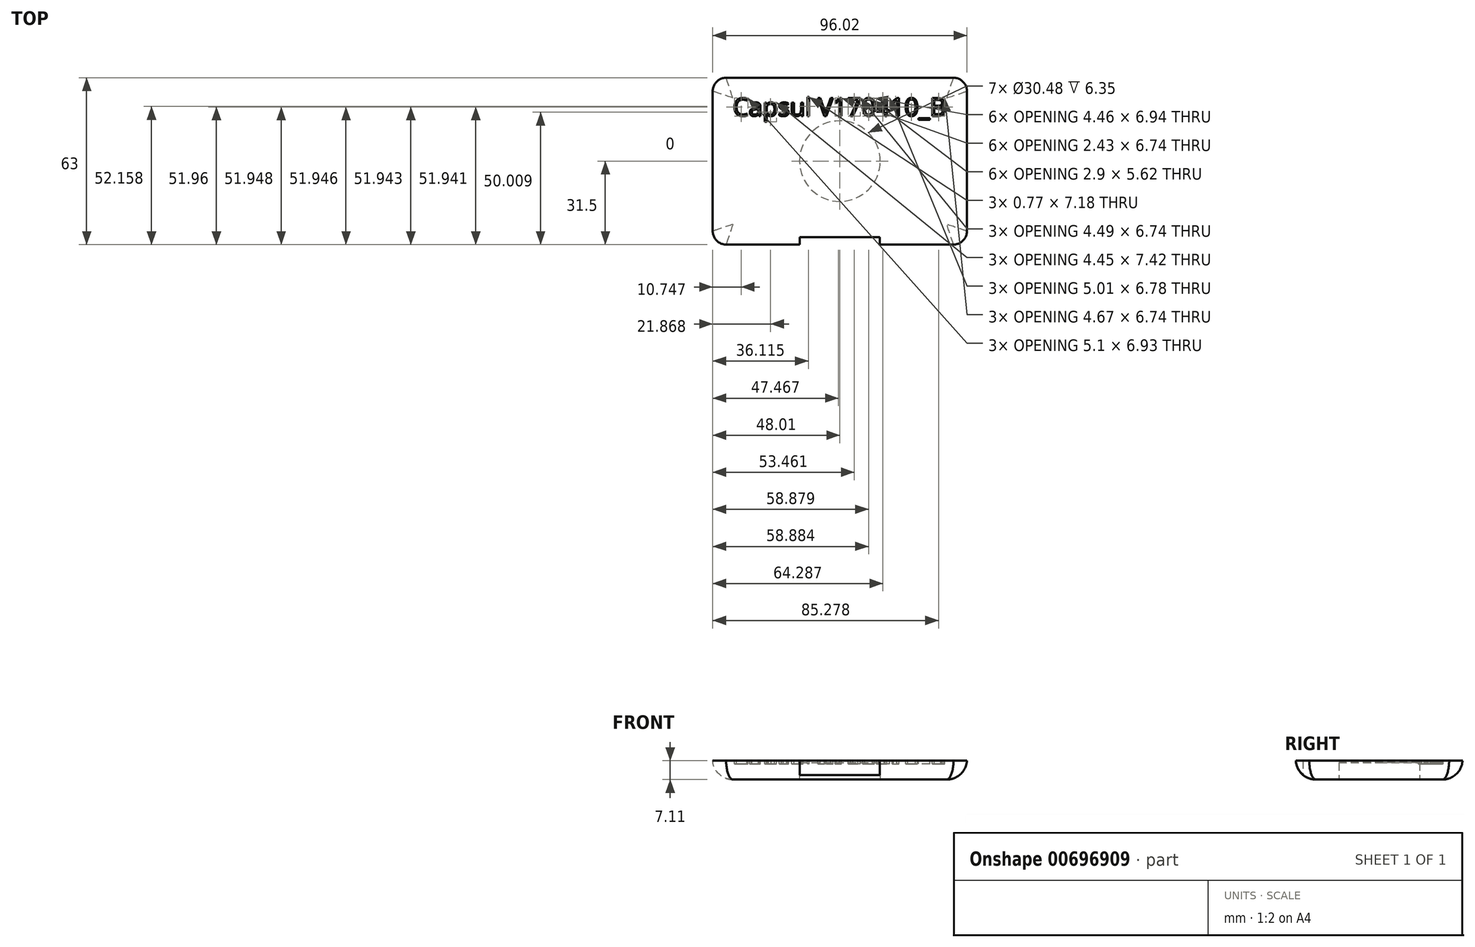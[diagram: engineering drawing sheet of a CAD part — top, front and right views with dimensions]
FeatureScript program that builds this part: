
annotation { "Feature Type Name" : "Feature", "Feature Type Description" : "" }
export const myFeature = defineFeature(function(context is Context, id is Id, definition is map)
    precondition{}
    {
        {
            var Q0;
            Q0=qCreatedBy(makeId("Top.planeOp"),FACE);
            var sketch = newSketch(context, id + "F0", { "sketchPlane" : qUnion([Q0])});
            skLineSegment(sketch, "E0.bottom", {"start": v(48, 31.5) * mm, "end": v(-48, 31.5) * mm});
            skLineSegment(sketch, "E0.top", {"start": v(48, -31.5) * mm, "end": v(-48, -31.5) * mm});
            skLineSegment(sketch, "E0.left", {"start": v(48, 31.5) * mm, "end": v(48, -31.5) * mm});
            skLineSegment(sketch, "E0.right", {"start": v(-48, 31.5) * mm, "end": v(-48, -31.5) * mm});
            skPoint(sketch, "E0.middle", {"position": v(0, 0) * mm});
            skSolve(sketch);
        }
        {
            var Q0;
            Q0=makeQuery(id+"F0.imprint","IMPRINT",FACE,{"disambiguationData":[TD([[makeQuery(id+"F0.imprint","IMPRINT",EDGE,{"derivedFrom":sQuery(id+"F0.wireOp",EDGE,"E0.bottom")}),1.0]])]});
            extrude(context, id + "F1", {"entities" : qUnion([Q0]), "depth" : 7.11 * mm, "offsetDistance" : 25.4 * mm});
        }
        {
            var Q0;
            Q0=makeQuery(id+"F1.opExtrude","CAP_FACE",FACE,{"disambiguationData":[OSD([sQuery(id+"F0.wireOp",EDGE,"E0.bottom"),sQuery(id+"F0.wireOp",EDGE,"E0.top"),sQuery(id+"F0.wireOp",EDGE,"E0.left"),sQuery(id+"F0.wireOp",EDGE,"E0.right")])],"isStart":true});
            fillet(context, id + "F2", {"entities" : qUnion([Q0]), "radius" : 7.62 * mm, "tangentPropagation" : true, "allowEdgeOverflow" : false});
        }
        {
            var Q0;
            Q0=makeQuery(id+"F2.opFillet","BLEND_EDGE",EDGE,{"blendedFrom":[makeQuery(id+"F1.opExtrude","CAP_EDGE",EDGE,{"disambiguationData":[OSD([sQuery(id+"F0.wireOp",EDGE,"E0.bottom")])],"isStart":true}),makeQuery(id+"F1.opExtrude","CAP_EDGE",EDGE,{"disambiguationData":[OSD([sQuery(id+"F0.wireOp",EDGE,"E0.right")])],"isStart":true})],"blendedInto":[]});
            var Q1;
            Q1=makeQuery(id+"F2.opFillet","BLEND_EDGE",EDGE,{"blendedFrom":[makeQuery(id+"F1.opExtrude","CAP_EDGE",EDGE,{"disambiguationData":[OSD([sQuery(id+"F0.wireOp",EDGE,"E0.top")])],"isStart":true}),makeQuery(id+"F1.opExtrude","CAP_EDGE",EDGE,{"disambiguationData":[OSD([sQuery(id+"F0.wireOp",EDGE,"E0.right")])],"isStart":true})],"blendedInto":[]});
            var Q2;
            Q2=makeQuery(id+"F2.opFillet","BLEND_EDGE",EDGE,{"blendedFrom":[makeQuery(id+"F1.opExtrude","CAP_EDGE",EDGE,{"disambiguationData":[OSD([sQuery(id+"F0.wireOp",EDGE,"E0.bottom")])],"isStart":true}),makeQuery(id+"F1.opExtrude","CAP_EDGE",EDGE,{"disambiguationData":[OSD([sQuery(id+"F0.wireOp",EDGE,"E0.left")])],"isStart":true})],"blendedInto":[]});
            var Q3;
            Q3=makeQuery(id+"F2.opFillet","BLEND_EDGE",EDGE,{"blendedFrom":[makeQuery(id+"F1.opExtrude","CAP_EDGE",EDGE,{"disambiguationData":[OSD([sQuery(id+"F0.wireOp",EDGE,"E0.top")])],"isStart":true}),makeQuery(id+"F1.opExtrude","CAP_EDGE",EDGE,{"disambiguationData":[OSD([sQuery(id+"F0.wireOp",EDGE,"E0.left")])],"isStart":true})],"blendedInto":[]});
            fillet(context, id + "F3", {"entities" : qUnion([Q0, Q1, Q2, Q3]), "radius" : 5.08 * mm, "tangentPropagation" : true, "allowEdgeOverflow" : false});
        }
        {
            var Q0;
            Q0=makeQuery(id+"F1.opExtrude","CAP_FACE",FACE,{"disambiguationData":[OSD([sQuery(id+"F0.wireOp",EDGE,"E0.bottom"),sQuery(id+"F0.wireOp",EDGE,"E0.top"),sQuery(id+"F0.wireOp",EDGE,"E0.left"),sQuery(id+"F0.wireOp",EDGE,"E0.right")])],"isStart":true});
            var sketch = newSketch(context, id + "F4", { "sketchPlane" : qUnion([Q0])});
            skCircle(sketch, "E1", {"center": v(0, 0) * mm, "radius": 15.24 * mm});
            skSolve(sketch);
        }
        {
            var Q0;
            Q0=qSketchRegion(id+"F4",true);
            extrude(context, id + "F5", {"entities" : qUnion([Q0]), "operationType" : NewBodyOperationType.REMOVE, "oppositeDirection" : true, "depth" : 6.35 * mm, "offsetDistance" : 25.4 * mm});
        }
        {
            var Q0;
            Q0=qCreatedBy(makeId("Top.planeOp"),FACE);
            var sketch = newSketch(context, id + "F6", { "sketchPlane" : qUnion([Q0])});
            skLineSegment(sketch, "E2.bottom", {"start": v(15.15, -28.75) * mm, "end": v(-15.15, -28.75) * mm});
            skLineSegment(sketch, "E2.top", {"start": v(15.15, -37.3) * mm, "end": v(-15.15, -37.3) * mm});
            skLineSegment(sketch, "E2.left", {"start": v(15.15, -28.75) * mm, "end": v(15.15, -37.3) * mm});
            skLineSegment(sketch, "E2.right", {"start": v(-15.15, -28.75) * mm, "end": v(-15.15, -37.3) * mm});
            skPoint(sketch, "E2.middle", {"position": v(0, -33.03) * mm});
            skSolve(sketch);
        }
        {
            var Q0;
            Q0=qSketchRegion(id+"F6",true);
            extrude(context, id + "F7", {"entities" : qUnion([Q0]), "operationType" : NewBodyOperationType.REMOVE, "depth" : 7.87 * mm, "offsetDistance" : 25.4 * mm});
        }
        {
            var Q0;
            Q0=makeQuery(id+"F1.opExtrude","CAP_FACE",FACE,{"disambiguationData":[OSD([sQuery(id+"F0.wireOp",EDGE,"E0.bottom"),sQuery(id+"F0.wireOp",EDGE,"E0.top"),sQuery(id+"F0.wireOp",EDGE,"E0.left"),sQuery(id+"F0.wireOp",EDGE,"E0.right")])],"isStart":false});
            var sketch = newSketch(context, id + "F8", { "sketchPlane" : qUnion([Q0])});
            skText(sketch, "E3", { "text": "Capsul V170410_B\n", "fontName": "OpenSans-Regular.ttf"});
            const initialGuessF8  = {"E3": [-0.04039, 0.01707, 1, 0, 0.0068]};
            skSetInitialGuess(sketch, initialGuessF8);
            skSolve(sketch);
        }
        {
            var Q0;
            Q0 = qSketchRegion(id + "F8", true);
            extrude(context, id + "F9", {"entities" : qUnion([Q0]), "operationType" : NewBodyOperationType.REMOVE, "oppositeDirection" : true, "depth" : 1.27 * mm, "offsetDistance" : 25.4 * mm});
        }
    });
